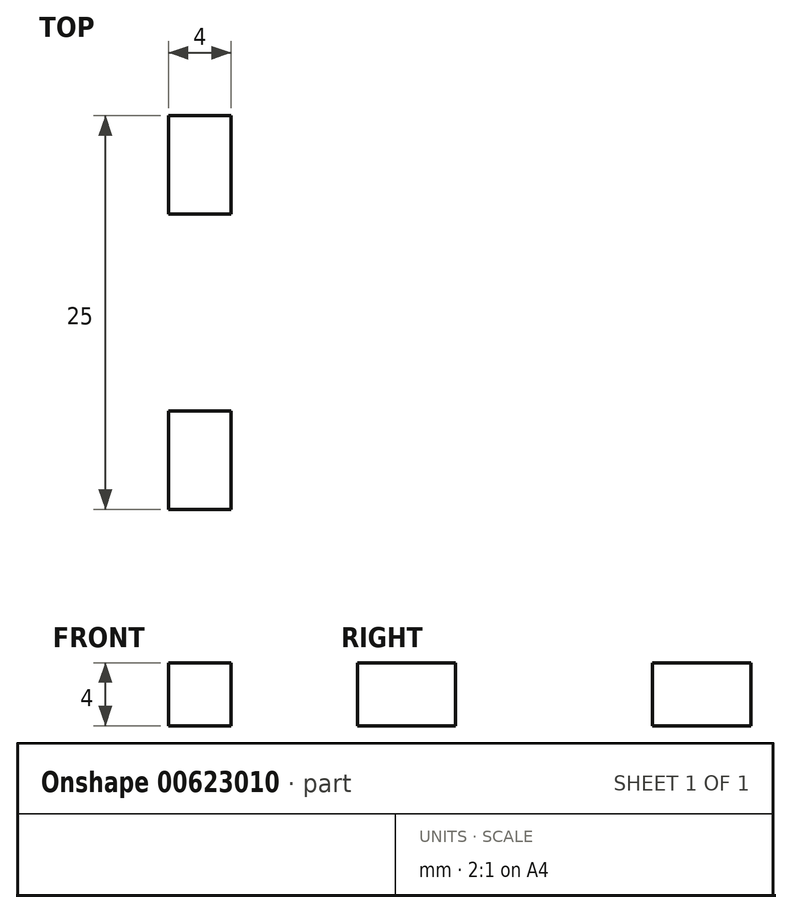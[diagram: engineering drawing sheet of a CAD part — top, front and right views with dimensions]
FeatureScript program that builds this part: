
annotation { "Feature Type Name" : "Feature", "Feature Type Description" : "" }
export const myFeature = defineFeature(function(context is Context, id is Id, definition is map)
    precondition{}
    {
        {
            var Q0;
            Q0=qCreatedBy(makeId("Top.planeOp"),FACE);
            var sketch = newSketch(context, id + "F0", { "sketchPlane" : qUnion([Q0])});
            skLineSegment(sketch, "E0.bottom", {"start": v(220, 11.24) * mm, "end": v(-80, 11.24) * mm});
            skLineSegment(sketch, "E0.top", {"start": v(220, 36.24) * mm, "end": v(-80, 36.24) * mm});
            skLineSegment(sketch, "E0.left", {"start": v(220, 11.24) * mm, "end": v(220, 36.24) * mm});
            skLineSegment(sketch, "E0.right", {"start": v(-80, 11.24) * mm, "end": v(-80, 36.24) * mm});
            skLineSegment(sketch, "E1.bottom", {"start": v(-60, 11.24) * mm, "end": v(-40, 11.24) * mm});
            skLineSegment(sketch, "E1.top", {"start": v(-60, 15.24) * mm, "end": v(-40, 15.24) * mm});
            skLineSegment(sketch, "E1.left", {"start": v(-60, 11.24) * mm, "end": v(-60, 15.24) * mm});
            skLineSegment(sketch, "E1.right", {"start": v(-40, 11.24) * mm, "end": v(-40, 15.24) * mm});
            skLineSegment(sketch, "E2.bottom", {"start": v(-20, 11.24) * mm, "end": v(0, 11.24) * mm});
            skLineSegment(sketch, "E2.top", {"start": v(-20, 15.24) * mm, "end": v(0, 15.24) * mm});
            skLineSegment(sketch, "E2.left", {"start": v(-20, 11.24) * mm, "end": v(-20, 15.24) * mm});
            skLineSegment(sketch, "E2.right", {"start": v(0, 11.24) * mm, "end": v(0, 15.24) * mm});
            skLineSegment(sketch, "E3.bottom", {"start": v(20, 11.24) * mm, "end": v(40, 11.24) * mm});
            skLineSegment(sketch, "E3.top", {"start": v(20, 15.24) * mm, "end": v(40, 15.24) * mm});
            skLineSegment(sketch, "E3.left", {"start": v(20, 11.24) * mm, "end": v(20, 15.24) * mm});
            skLineSegment(sketch, "E3.right", {"start": v(40, 11.24) * mm, "end": v(40, 15.24) * mm});
            skLineSegment(sketch, "E4.bottom", {"start": v(60, 11.24) * mm, "end": v(80, 11.24) * mm});
            skLineSegment(sketch, "E4.top", {"start": v(60, 15.24) * mm, "end": v(80, 15.24) * mm});
            skLineSegment(sketch, "E4.left", {"start": v(60, 11.24) * mm, "end": v(60, 15.24) * mm});
            skLineSegment(sketch, "E4.right", {"start": v(80, 11.24) * mm, "end": v(80, 15.24) * mm});
            skLineSegment(sketch, "E5.bottom", {"start": v(100, 15.24) * mm, "end": v(120, 15.24) * mm});
            skLineSegment(sketch, "E5.top", {"start": v(100, 11.24) * mm, "end": v(120, 11.24) * mm});
            skLineSegment(sketch, "E5.left", {"start": v(100, 15.24) * mm, "end": v(100, 11.24) * mm});
            skLineSegment(sketch, "E5.right", {"start": v(120, 15.24) * mm, "end": v(120, 11.24) * mm});
            skLineSegment(sketch, "E6.bottom", {"start": v(140, 15.24) * mm, "end": v(160, 15.24) * mm});
            skLineSegment(sketch, "E6.top", {"start": v(140, 11.24) * mm, "end": v(160, 11.24) * mm});
            skLineSegment(sketch, "E6.left", {"start": v(140, 15.24) * mm, "end": v(140, 11.24) * mm});
            skLineSegment(sketch, "E6.right", {"start": v(160, 15.24) * mm, "end": v(160, 11.24) * mm});
            skLineSegment(sketch, "E7.bottom", {"start": v(180, 15.24) * mm, "end": v(200, 15.24) * mm});
            skLineSegment(sketch, "E7.top", {"start": v(180, 11.24) * mm, "end": v(200, 11.24) * mm});
            skLineSegment(sketch, "E7.left", {"start": v(180, 15.24) * mm, "end": v(180, 11.24) * mm});
            skLineSegment(sketch, "E7.right", {"start": v(200, 15.24) * mm, "end": v(200, 11.24) * mm});
            skLineSegment(sketch, "E8.bottom", {"start": v(-80, 11.24) * mm, "end": v(-76, 11.24) * mm});
            skLineSegment(sketch, "E8.top", {"start": v(-80, 17.5) * mm, "end": v(-76, 17.5) * mm});
            skLineSegment(sketch, "E8.left", {"start": v(-80, 11.24) * mm, "end": v(-80, 17.5) * mm});
            skLineSegment(sketch, "E8.right", {"start": v(-76, 11.24) * mm, "end": v(-76, 17.5) * mm});
            skLineSegment(sketch, "E9.bottom", {"start": v(-80, 36.24) * mm, "end": v(-76, 36.24) * mm});
            skLineSegment(sketch, "E9.top", {"start": v(-80, 30) * mm, "end": v(-76, 30) * mm});
            skLineSegment(sketch, "E9.left", {"start": v(-80, 36.24) * mm, "end": v(-80, 30) * mm});
            skLineSegment(sketch, "E9.right", {"start": v(-76, 36.24) * mm, "end": v(-76, 30) * mm});
            skLineSegment(sketch, "E10.bottom", {"start": v(220, 36.24) * mm, "end": v(216, 36.24) * mm});
            skLineSegment(sketch, "E10.top", {"start": v(220, 30) * mm, "end": v(216, 30) * mm});
            skLineSegment(sketch, "E10.left", {"start": v(220, 36.24) * mm, "end": v(220, 30) * mm});
            skLineSegment(sketch, "E10.right", {"start": v(216, 36.24) * mm, "end": v(216, 30) * mm});
            skLineSegment(sketch, "E11.bottom", {"start": v(220, 11.24) * mm, "end": v(216, 11.24) * mm});
            skLineSegment(sketch, "E11.top", {"start": v(220, 17.5) * mm, "end": v(216, 17.5) * mm});
            skLineSegment(sketch, "E11.left", {"start": v(220, 11.24) * mm, "end": v(220, 17.5) * mm});
            skLineSegment(sketch, "E11.right", {"start": v(216, 11.24) * mm, "end": v(216, 17.5) * mm});
            skLineSegment(sketch, "E12.bottom", {"start": v(-60, 36.24) * mm, "end": v(-40, 36.24) * mm});
            skLineSegment(sketch, "E12.top", {"start": v(-60, 32.24) * mm, "end": v(-40, 32.24) * mm});
            skLineSegment(sketch, "E12.left", {"start": v(-60, 36.24) * mm, "end": v(-60, 32.24) * mm});
            skLineSegment(sketch, "E12.right", {"start": v(-40, 36.24) * mm, "end": v(-40, 32.24) * mm});
            skLineSegment(sketch, "E13.bottom", {"start": v(-20, 36.24) * mm, "end": v(0, 36.24) * mm});
            skLineSegment(sketch, "E13.top", {"start": v(-20, 32.24) * mm, "end": v(0, 32.24) * mm});
            skLineSegment(sketch, "E13.left", {"start": v(-20, 36.24) * mm, "end": v(-20, 32.24) * mm});
            skLineSegment(sketch, "E13.right", {"start": v(0, 36.24) * mm, "end": v(0, 32.24) * mm});
            skLineSegment(sketch, "E14.bottom", {"start": v(20, 36.24) * mm, "end": v(40, 36.24) * mm});
            skLineSegment(sketch, "E14.top", {"start": v(20, 32.24) * mm, "end": v(40, 32.24) * mm});
            skLineSegment(sketch, "E14.left", {"start": v(20, 36.24) * mm, "end": v(20, 32.24) * mm});
            skLineSegment(sketch, "E14.right", {"start": v(40, 36.24) * mm, "end": v(40, 32.24) * mm});
            skLineSegment(sketch, "E15.bottom", {"start": v(60, 36.24) * mm, "end": v(80, 36.24) * mm});
            skLineSegment(sketch, "E15.top", {"start": v(60, 32.24) * mm, "end": v(80, 32.24) * mm});
            skLineSegment(sketch, "E15.left", {"start": v(60, 36.24) * mm, "end": v(60, 32.24) * mm});
            skLineSegment(sketch, "E15.right", {"start": v(80, 36.24) * mm, "end": v(80, 32.24) * mm});
            skLineSegment(sketch, "E16.bottom", {"start": v(100, 36.24) * mm, "end": v(120, 36.24) * mm});
            skLineSegment(sketch, "E16.top", {"start": v(100, 32.24) * mm, "end": v(120, 32.24) * mm});
            skLineSegment(sketch, "E16.left", {"start": v(100, 36.24) * mm, "end": v(100, 32.24) * mm});
            skLineSegment(sketch, "E16.right", {"start": v(120, 36.24) * mm, "end": v(120, 32.24) * mm});
            skLineSegment(sketch, "E17.bottom", {"start": v(140, 36.24) * mm, "end": v(160, 36.24) * mm});
            skLineSegment(sketch, "E17.top", {"start": v(140, 32.24) * mm, "end": v(160, 32.24) * mm});
            skLineSegment(sketch, "E17.left", {"start": v(140, 36.24) * mm, "end": v(140, 32.24) * mm});
            skLineSegment(sketch, "E17.right", {"start": v(160, 36.24) * mm, "end": v(160, 32.24) * mm});
            skLineSegment(sketch, "E18.bottom", {"start": v(180, 36.24) * mm, "end": v(200, 36.24) * mm});
            skLineSegment(sketch, "E18.top", {"start": v(180, 32.24) * mm, "end": v(200, 32.24) * mm});
            skLineSegment(sketch, "E18.left", {"start": v(180, 36.24) * mm, "end": v(180, 32.24) * mm});
            skLineSegment(sketch, "E18.right", {"start": v(200, 36.24) * mm, "end": v(200, 32.24) * mm});
            skSolve(sketch);
        }
        {
            var Q0;
            Q0=makeQuery(id+"F0.imprint","IMPRINT",FACE,{"disambiguationData":[TD([[makeQuery(id+"F0.imprint","IMPRINT",EDGE,{"derivedFrom":sQuery(id+"F0.wireOp",EDGE,"E0.left")}),1.0]])]});
            extrude(context, id + "F1", {"entities" : qUnion([Q0]), "depth" : 4 * mm, "offsetDistance" : 25 * mm});
        }
    });
